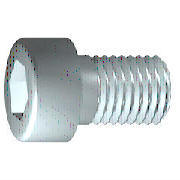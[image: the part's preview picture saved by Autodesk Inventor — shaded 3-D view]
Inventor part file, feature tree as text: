
AUTODESK INVENTOR PART (.ipt)
format: ipt  version: 2025 (Build 290162010, 162A)  size: 190,464 bytes
history: native  units: mm (DEFAULTED — no unit token found)
features: extrude x1, plane x1, fillet x1
ambient origin geometry x7: Origin, YZ Plane, XY Plane, X Axis, Y Axis, Z Axis, Center Point
bodies: Solid1 (feature_tree), Body (feature_tree)
feature tree (3):
  extrude  "Slot"  Depth=18.0mm
  plane  "Work Plane1"
  fillet  "Fillet2"  Radius=0.306825mm
